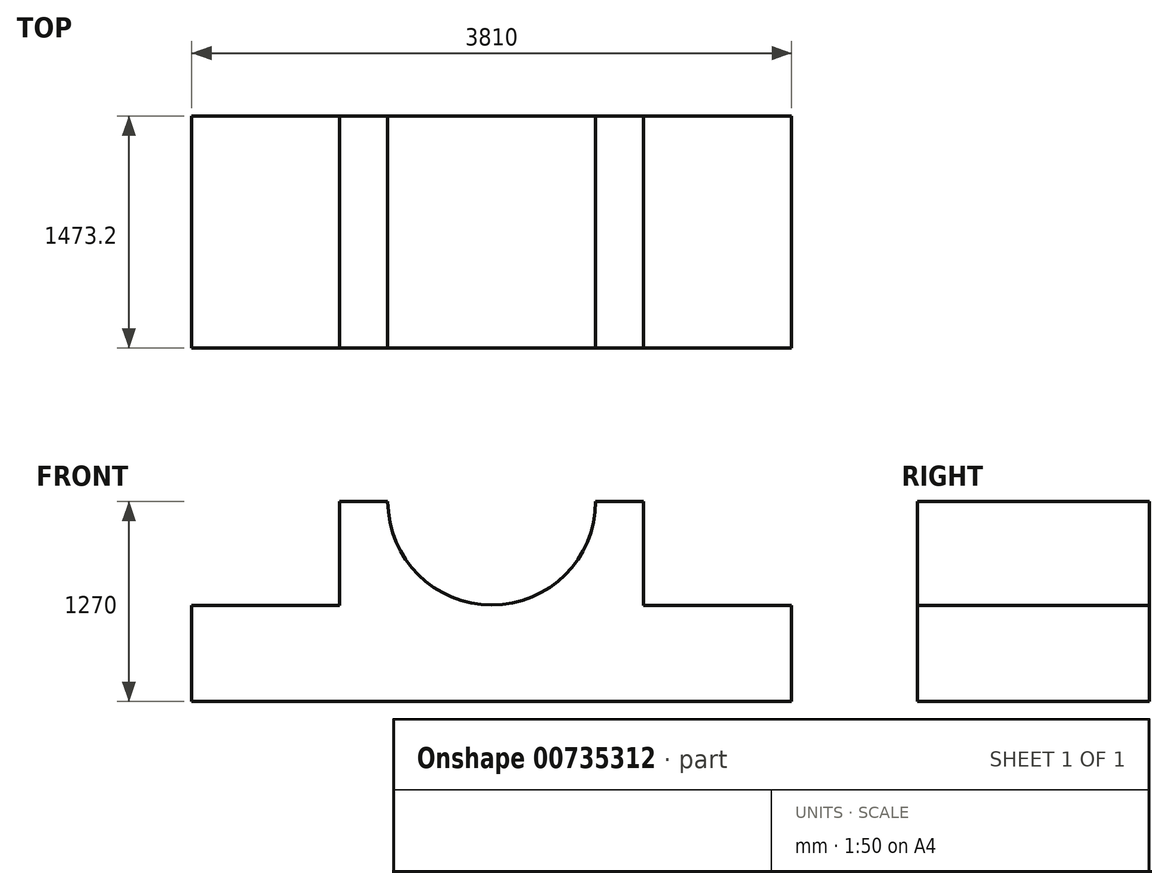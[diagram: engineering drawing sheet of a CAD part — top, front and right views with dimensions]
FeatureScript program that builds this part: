
annotation { "Feature Type Name" : "Feature", "Feature Type Description" : "" }
export const myFeature = defineFeature(function(context is Context, id is Id, definition is map)
    precondition{}
    {
        {
            var Q0;
            Q0=qCreatedBy(makeId("Front.planeOp"),FACE);
            var sketch = newSketch(context, id + "F0", { "sketchPlane" : qUnion([Q0])});
            skLineSegment(sketch, "E0", {"start": v(0, 0) * mm, "end": v(0, 609.6) * mm});
            skLineSegment(sketch, "E1", {"start": v(0, 609.6) * mm, "end": v(939.8, 609.6) * mm});
            skLineSegment(sketch, "E2", {"start": v(939.8, 609.6) * mm, "end": v(939.8, 1270) * mm});
            skLineSegment(sketch, "E3", {"start": v(939.8, 1270) * mm, "end": v(1244.6, 1270) * mm});
            skLineSegment(sketch, "E4", {"start": v(0, 0) * mm, "end": v(3810, 0) * mm});
            skLineSegment(sketch, "E5", {"start": v(3810, 0) * mm, "end": v(3810, 609.6) * mm});
            skLineSegment(sketch, "E6", {"start": v(3810, 609.6) * mm, "end": v(2870.2, 609.6) * mm});
            skLineSegment(sketch, "E7", {"start": v(2870.2, 609.6) * mm, "end": v(2870.2, 1270) * mm});
            skLineSegment(sketch, "E8", {"start": v(2870.2, 1270) * mm, "end": v(2565.4, 1270) * mm});
            skArc(sketch, "E9", {"start": v(1244.6, 1270) * mm, "mid": v(1905, 611.96) * mm, "end": v(2565.4, 1270) * mm});
            skSolve(sketch);
        }
        {
            var Q0;
            Q0=makeQuery(id+"F0.imprint","IMPRINT",FACE,{"disambiguationData":[TD([[makeQuery(id+"F0.imprint","IMPRINT",EDGE,{"derivedFrom":sQuery(id+"F0.wireOp",EDGE,"E0")}),-1.0]])]});
            extrude(context, id + "F1", {"entities" : qUnion([Q0]), "depth" : 1473.2 * mm, "offsetDistance" : 25.4 * mm});
        }
    });
